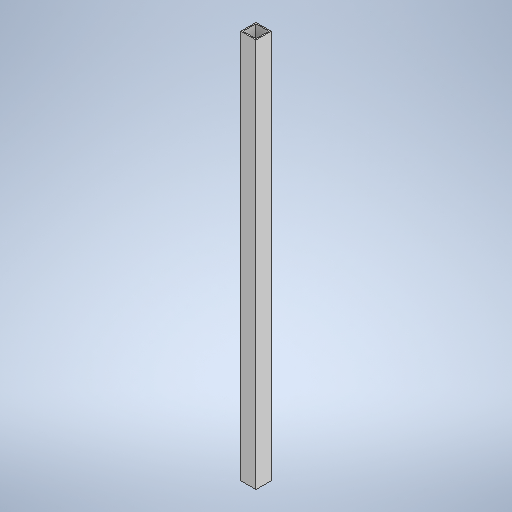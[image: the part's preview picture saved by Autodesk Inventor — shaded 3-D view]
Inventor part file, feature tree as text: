
AUTODESK INVENTOR PART (.ipt)
format: ipt  version: 2025 (Build 290162000, 162)  size: 259,072 bytes
history: native  units: in
note: dims shown in document units (in); Inventor stores cm internally (conversion verified against a paired STEP export)
features: extrude x1, sketch x1
ambient origin geometry x8: Origin, YZ Plane, XZ Plane, XY Plane, X Axis, Y Axis, Z Axis, Center Point
bodies: Solid1 (feature_tree)
feature tree (2):
  extrude  "Extrusion1"  Depth=1.5748in
  sketch  "Sketch1"  dims[d0=1.5748in d1=1.5748in d2=1.3386in d3=1.3386in d4=0.1181in d5=40.5512in d6=0.0in]
